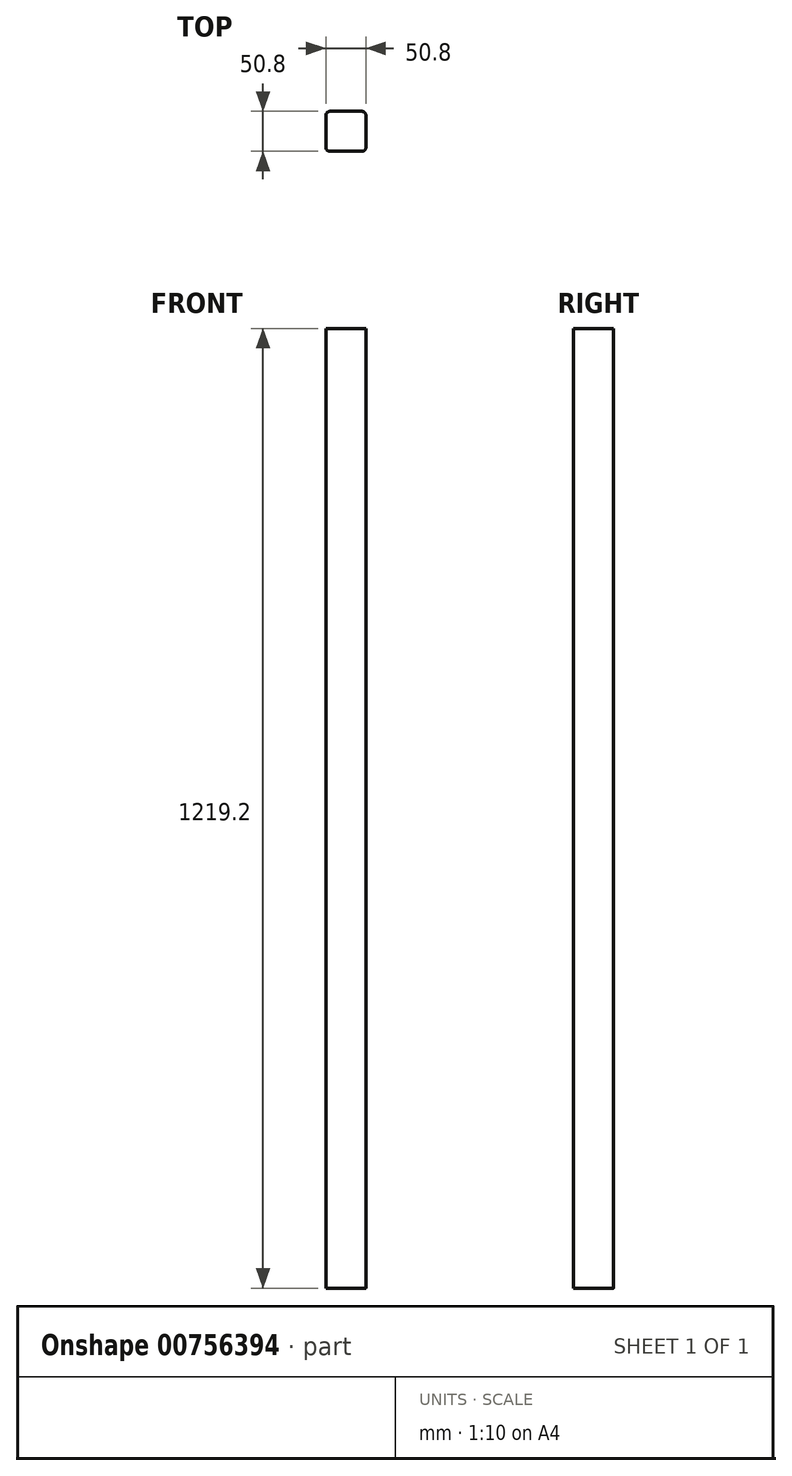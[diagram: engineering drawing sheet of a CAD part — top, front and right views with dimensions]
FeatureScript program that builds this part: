
annotation { "Feature Type Name" : "Feature", "Feature Type Description" : "" }
export const myFeature = defineFeature(function(context is Context, id is Id, definition is map)
    precondition{}
    {
        {
            var Q0;
            Q0=qCreatedBy(makeId("Top.planeOp"),FACE);
            var sketch = newSketch(context, id + "F0", { "sketchPlane" : qUnion([Q0])});
            skLineSegment(sketch, "E0.bottom", {"start": v(5, 0) * mm, "end": v(45.8, 0) * mm});
            skLineSegment(sketch, "E0.top", {"start": v(5, 50.8) * mm, "end": v(45.8, 50.8) * mm});
            skLineSegment(sketch, "E0.left", {"start": v(0, 5) * mm, "end": v(0, 45.8) * mm});
            skLineSegment(sketch, "E0.right", {"start": v(50.8, 5) * mm, "end": v(50.8, 45.8) * mm});
            skPoint(sketch, "E1.visualSharp", {"position": v(0, 50.8) * mm});
            skArc(sketch, "E1.filletArc", {"start": v(5, 50.8) * mm, "mid": v(1.46, 49.34) * mm, "end": v(0, 45.8) * mm});
            skPoint(sketch, "E2.visualSharp", {"position": v(50.8, 50.8) * mm});
            skArc(sketch, "E2.filletArc", {"start": v(50.8, 45.8) * mm, "mid": v(49.34, 49.34) * mm, "end": v(45.8, 50.8) * mm});
            skPoint(sketch, "E3.visualSharp", {"position": v(50.8, 0) * mm});
            skArc(sketch, "E3.filletArc", {"start": v(45.8, 0) * mm, "mid": v(49.34, 1.46) * mm, "end": v(50.8, 5) * mm});
            skPoint(sketch, "E4.visualSharp", {"position": v(0, 0) * mm});
            skArc(sketch, "E4.filletArc", {"start": v(0, 5) * mm, "mid": v(1.46, 1.46) * mm, "end": v(5, 0) * mm});
            skSolve(sketch);
        }
        {
            var Q0;
            Q0=makeQuery(id+"F0.imprint","IMPRINT",FACE,{"disambiguationData":[TD([[makeQuery(id+"F0.imprint","IMPRINT",EDGE,{"derivedFrom":sQuery(id+"F0.wireOp",EDGE,"E0.bottom")}),1.0]])]});
            extrude(context, id + "F1", {"entities" : qUnion([Q0]), "depth" : 1219.2 * mm, "offsetDistance" : 25.4 * mm});
        }
    });
